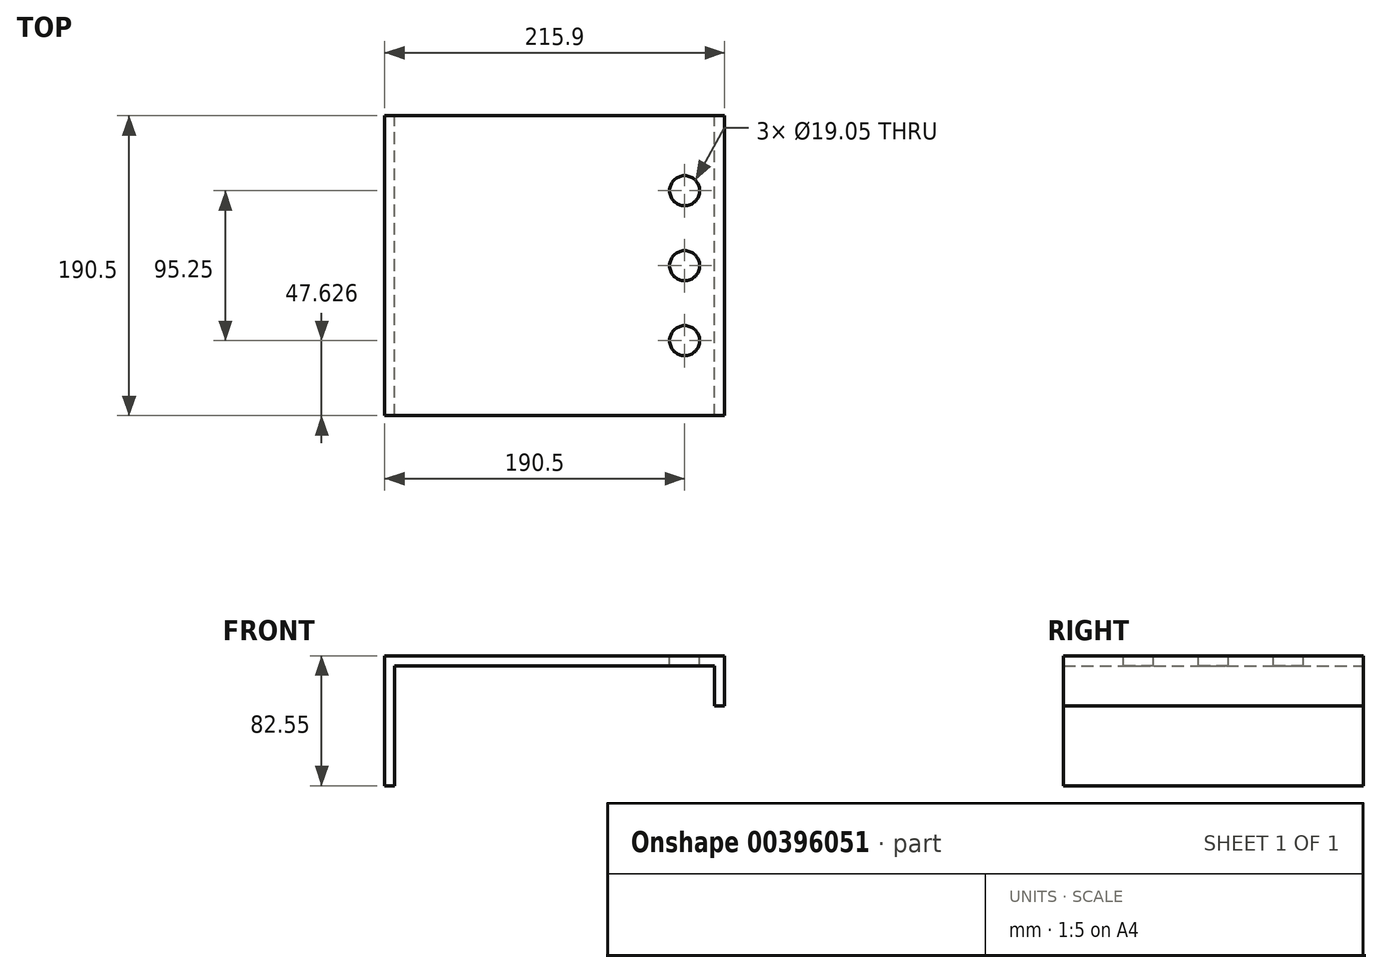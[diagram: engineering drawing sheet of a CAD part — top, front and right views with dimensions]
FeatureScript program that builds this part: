
annotation { "Feature Type Name" : "Feature", "Feature Type Description" : "" }
export const myFeature = defineFeature(function(context is Context, id is Id, definition is map)
    precondition{}
    {
        {
            var Q0;
            Q0=qCreatedBy(makeId("Top.planeOp"),FACE);
            var sketch = newSketch(context, id + "F0", { "sketchPlane" : qUnion([Q0])});
            skLineSegment(sketch, "E0.bottom", {"start": v(-66.5, 130.9) * mm, "end": v(149.4, 130.9) * mm});
            skLineSegment(sketch, "E0.top", {"start": v(-66.5, -59.6) * mm, "end": v(149.4, -59.6) * mm});
            skLineSegment(sketch, "E0.left", {"start": v(-66.5, 130.9) * mm, "end": v(-66.5, -59.6) * mm});
            skLineSegment(sketch, "E0.right", {"start": v(149.4, 130.9) * mm, "end": v(149.4, -59.6) * mm});
            skSolve(sketch);
        }
        {
            var Q0;
            Q0 = qSketchRegion(id + "F0", true);
            extrude(context, id + "F1", {"entities" : qUnion([Q0]), "depth" : 6.35 * mm});
        }
        {
            var Q0;
            Q0=makeQuery(id+"F1.opExtrude","CAP_FACE",FACE,{"disambiguationData":[OSD([sQuery(id+"F0.wireOp",EDGE,"E0.bottom"),sQuery(id+"F0.wireOp",EDGE,"E0.top"),sQuery(id+"F0.wireOp",EDGE,"E0.left"),sQuery(id+"F0.wireOp",EDGE,"E0.right")])],"isStart":false});
            var sketch = newSketch(context, id + "F2", { "sketchPlane" : qUnion([Q0])});
            skCircle(sketch, "E1", {"center": v(124, 83.27) * mm, "radius": 9.53 * mm});
            skCircle(sketch, "E2", {"center": v(124, 35.64) * mm, "radius": 9.53 * mm});
            skCircle(sketch, "E3", {"center": v(124, -11.98) * mm, "radius": 9.53 * mm});
            skSolve(sketch);
        }
        {
            var Q0;
            Q0 = qSketchRegion(id + "F2", true);
            extrude(context, id + "F3", {"entities" : qUnion([Q0]), "operationType" : NewBodyOperationType.REMOVE, "oppositeDirection" : true, "depth" : 25.4 * mm});
        }
        {
            var Q0;
            Q0=makeQuery(id+"F1.opExtrude","CAP_FACE",FACE,{"disambiguationData":[OSD([sQuery(id+"F0.wireOp",EDGE,"E0.bottom"),sQuery(id+"F0.wireOp",EDGE,"E0.top"),sQuery(id+"F0.wireOp",EDGE,"E0.left"),sQuery(id+"F0.wireOp",EDGE,"E0.right")])],"isStart":true});
            var sketch = newSketch(context, id + "F4", { "sketchPlane" : qUnion([Q0])});
            skLineSegment(sketch, "E4.bottom", {"start": v(-66.5, 59.6) * mm, "end": v(-60.15, 59.6) * mm});
            skLineSegment(sketch, "E4.top", {"start": v(-66.5, -130.9) * mm, "end": v(-60.15, -130.9) * mm});
            skLineSegment(sketch, "E4.left", {"start": v(-66.5, 59.6) * mm, "end": v(-66.5, -130.9) * mm});
            skLineSegment(sketch, "E4.right", {"start": v(-60.15, 59.6) * mm, "end": v(-60.15, -130.9) * mm});
            skLineSegment(sketch, "E5.bottom", {"start": v(149.4, 59.6) * mm, "end": v(143.05, 59.6) * mm});
            skLineSegment(sketch, "E5.top", {"start": v(149.4, -130.9) * mm, "end": v(143.05, -130.9) * mm});
            skLineSegment(sketch, "E5.left", {"start": v(149.4, 59.6) * mm, "end": v(149.4, -130.9) * mm});
            skLineSegment(sketch, "E5.right", {"start": v(143.05, 59.6) * mm, "end": v(143.05, -130.9) * mm});
            skSolve(sketch);
        }
        {
            var Q0;
            Q0=makeQuery(id+"F4.imprint","IMPRINT",FACE,{"disambiguationData":[TD([[makeQuery(id+"F4.imprint","IMPRINT",EDGE,{"derivedFrom":sQuery(id+"F4.wireOp",EDGE,"E4.bottom")}),-1.0]])]});
            extrude(context, id + "F5", {"entities" : qUnion([Q0]), "operationType" : NewBodyOperationType.ADD, "depth" : 76.2 * mm});
        }
        {
            var Q0;
            Q0=makeQuery(id+"F1.opExtrude","CAP_FACE",FACE,{"disambiguationData":[OSD([sQuery(id+"F0.wireOp",EDGE,"E0.bottom"),sQuery(id+"F0.wireOp",EDGE,"E0.top"),sQuery(id+"F0.wireOp",EDGE,"E0.left"),sQuery(id+"F0.wireOp",EDGE,"E0.right")])],"isStart":true});
            var sketch = newSketch(context, id + "F6", { "sketchPlane" : qUnion([Q0])});
            skLineSegment(sketch, "E6.bottom", {"start": v(149.4, 59.6) * mm, "end": v(143.05, 59.6) * mm});
            skLineSegment(sketch, "E6.top", {"start": v(149.4, -130.9) * mm, "end": v(143.05, -130.9) * mm});
            skLineSegment(sketch, "E6.left", {"start": v(149.4, 59.6) * mm, "end": v(149.4, -130.9) * mm});
            skLineSegment(sketch, "E6.right", {"start": v(143.05, 59.6) * mm, "end": v(143.05, -130.9) * mm});
            skSolve(sketch);
        }
        {
            var Q0;
            Q0 = qSketchRegion(id + "F6", true);
            extrude(context, id + "F7", {"entities" : qUnion([Q0]), "operationType" : NewBodyOperationType.ADD, "depth" : 25.4 * mm});
        }
    });
